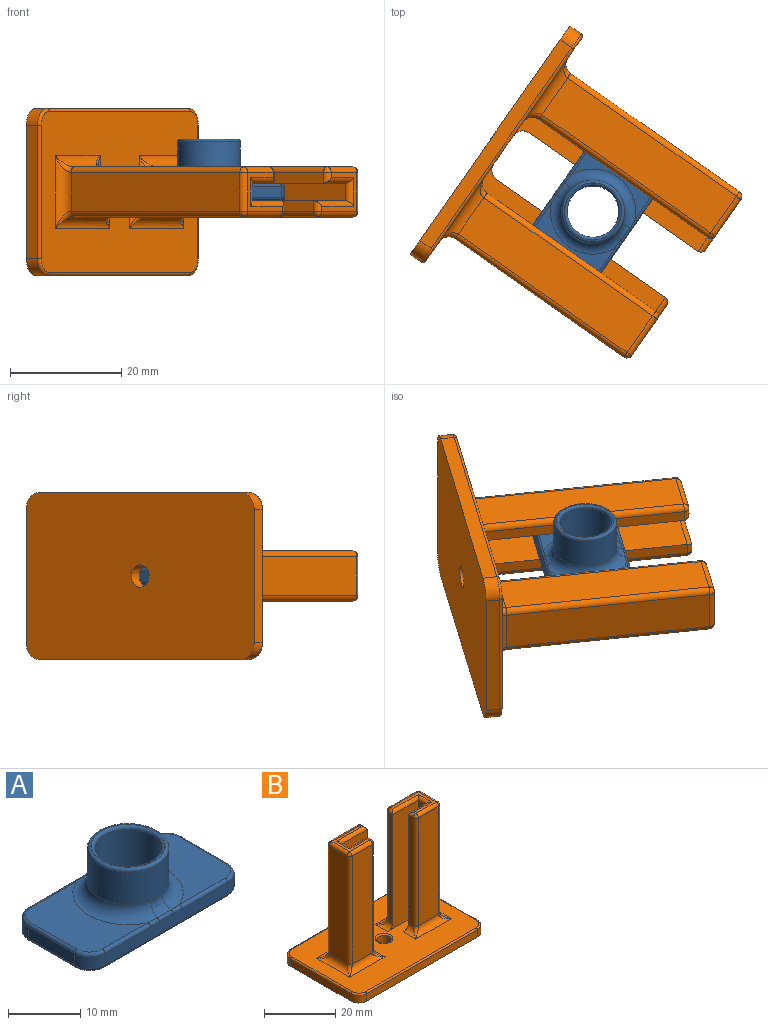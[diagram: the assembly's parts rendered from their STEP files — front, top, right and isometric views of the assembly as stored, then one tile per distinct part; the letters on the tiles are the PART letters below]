
ASSEMBLY  parts=2 mates=1
PART A: 45 faces, bbox 30.5x19.3x11 mm
  f0: plane 14x11.44mm, normal (0,0,1), area 111.3mm2, adj f15,f18,f19,f20,f22,f24
  f1: plane 9x2mm, normal (1,0,0), area 18mm2, adj f2,f9,f31,f38
  f2: cylinder r=3mm len=3mm, axis (0,0,-1), area 9.4mm2, adj f1,f3,f33,f40
  f3: plane 24x2.08mm, normal (0,1,0), area 48.3mm2, adj f2,f4,f24,f26,f28,f30,f32,f41
  f4: cylinder r=3mm len=3mm, axis (0,0,-1), area 9.4mm2, adj f3,f5,f22,f39
  f5: plane 9x2mm, normal (-1,0,0), area 18mm2, adj f4,f6,f20,f37
  f6: cylinder r=3mm len=3mm, axis (0,0,-1), area 9.4mm2, adj f5,f7,f18,f35
  f7: plane 24x2.08mm, normal (0,-1,0), area 48.3mm2, adj f6,f9,f19,f21,f23,f25,f27,f34
  f8: cylinder r=4.6mm len=10mm, axis (0,0,-1), area 289mm2, adj f42,f44
  f9: cylinder r=3mm len=3mm, axis (0,0,-1), area 9.4mm2, adj f1,f7,f29,f36
  f10: plane 14x11.44mm, normal (0,0,1), area 111.3mm2, adj f16,f27,f29,f31,f32,f33
  f11: plane 29x14mm, normal (0,0,-1), area 318.9mm2, adj f34,f35,f36,f37,f38,f39,f40,f41
  f12: cylinder r=5.64mm len=11.28mm, axis (0,0,-1), area 194.9mm2, adj f14,f15,f16,f17,f43
  f13: plane 10.28x10.28mm, normal (0,0,1), area 1.3mm2, adj f42,f43
  f14: bspline ~4.14x2.15mm, area 6.3mm2, adj f12,f15,f16,f28
  f15: torus R=7.64mm, axis (0,0,1), area 54.5mm2, adj f0,f12,f14,f17,f21,f26
  f16: torus R=7.64mm, axis (0,0,1), area 54.5mm2, adj f10,f12,f14,f17,f25,f30
  f17: bspline ~4.14x2.15mm, area 6.3mm2, adj f12,f15,f16,f23
  f18: torus R=2.5mm, axis (0,0,1), area 3.5mm2, adj f0,f6,f19,f20
  f19: cylinder r=0.5mm len=8.94mm, axis (-1,0,0), area 7mm2, adj f0,f7,f18,f21
  f20: cylinder r=0.5mm len=9mm, axis (0,1,0), area 7.1mm2, adj f0,f5,f18,f22
  f21: bspline ~3.04x0.56mm, area 1.2mm2, adj f7,f15,f19,f23
  f22: torus R=2.5mm, axis (0,0,1), area 3.5mm2, adj f0,f4,f20,f24
  f23: bspline ~3.6x0.53mm, area 1.8mm2, adj f7,f17,f21,f25
  f24: cylinder r=0.5mm len=8.94mm, axis (1,0,0), area 7mm2, adj f0,f3,f22,f26
  f25: bspline ~3.41x0.59mm, area 1.2mm2, adj f7,f16,f23,f27
  f26: bspline ~3.41x0.59mm, area 1.2mm2, adj f3,f15,f24,f28
  f27: cylinder r=0.5mm len=8.94mm, axis (-1,0,0), area 7mm2, adj f7,f10,f25,f29
  f28: bspline ~3.6x0.53mm, area 1.8mm2, adj f3,f14,f26,f30
  f29: torus R=2.5mm, axis (0,0,1), area 3.5mm2, adj f9,f10,f27,f31
  f30: bspline ~3.04x0.56mm, area 1.2mm2, adj f3,f16,f28,f32
  f31: cylinder r=0.5mm len=9mm, axis (0,-1,0), area 7.1mm2, adj f1,f10,f29,f33
  f32: cylinder r=0.5mm len=8.94mm, axis (1,0,0), area 7mm2, adj f3,f10,f30,f33
  f33: torus R=2.5mm, axis (0,0,1), area 3.5mm2, adj f2,f10,f31,f32
  f34: cylinder r=0.5mm len=24mm, axis (1,0,0), area 18.8mm2, adj f7,f11,f35,f36
  f35: torus R=2.5mm, axis (0,0,1), area 3.5mm2, adj f6,f11,f34,f37
  f36: torus R=2.5mm, axis (0,0,1), area 3.5mm2, adj f9,f11,f34,f38
  f37: cylinder r=0.5mm len=9mm, axis (0,-1,0), area 7.1mm2, adj f5,f11,f35,f39
  f38: cylinder r=0.5mm len=9mm, axis (0,1,0), area 7.1mm2, adj f1,f11,f36,f40
  f39: torus R=2.5mm, axis (0,0,1), area 3.5mm2, adj f4,f11,f37,f41
  f40: torus R=2.5mm, axis (0,0,1), area 3.5mm2, adj f2,f11,f38,f41
  f41: cylinder r=0.5mm len=24mm, axis (-1,0,0), area 18.8mm2, adj f3,f11,f39,f40
  f42: torus R=5.1mm, axis (0,0,1), area 23.6mm2, adj f8,f13
  f43: torus R=5.14mm, axis (0,0,1), area 26.9mm2, adj f12,f13
  f44: torus R=5.1mm, axis (0,0,1), area 23.6mm2, adj f8,f11
PART B: 88 faces, bbox 50.5x30.5x43 mm
  f0: plane 24x2.5mm, normal (1,0,0), area 60mm2, adj f1,f8,f10,f83
  f1: cylinder r=3mm len=3mm, axis (0,0,-1), area 11.8mm2, adj f0,f2,f10,f81
  f2: plane 44x2.5mm, normal (0,1,0), area 110mm2, adj f1,f3,f10,f79
  f3: cylinder r=3mm len=3mm, axis (0,0,-1), area 11.8mm2, adj f2,f4,f10,f80
  f4: plane 24x2.5mm, normal (-1,0,0), area 60mm2, adj f3,f5,f10,f82
  f5: cylinder r=3mm len=3mm, axis (0,0,-1), area 11.8mm2, adj f4,f6,f10,f84
  f6: plane 44x2.5mm, normal (0,-1,0), area 110mm2, adj f5,f8,f10,f86
  f7: cylinder r=2mm len=4mm, axis (0,0,-1), area 31.4mm2, adj f10,f87
  f8: cylinder r=3mm len=3mm, axis (0,0,-1), area 11.8mm2, adj f0,f6,f10,f85
  f9: plane 49x29mm, normal (0,0,1), area 1060.2mm2, adj f15,f16,f17,f24,f25,f26,f29,f30
  f10: plane 50x30mm, normal (0,0,-1), area 1479.7mm2, adj f0,f1,f2,f3,f4,f5,f6,f7
  f11: plane 37x11mm, normal (0,1,0), area 407mm2, adj f36,f71,f75,f77
  f12: plane 37x7mm, normal (-1,0,0), area 259mm2, adj f38,f65,f70,f71
  f13: plane 37x8mm, normal (0,-1,0), area 296mm2, adj f37,f60,f64,f65
  f14: plane 37x1.9mm, normal (1,0,0), area 70.3mm2, adj f15,f35,f60,f63
  f15: plane 39x9mm, normal (0,1,0), area 273.9mm2, adj f9,f14,f16,f35,f66
  f16: plane 39x3.2mm, normal (1,0,0), area 124.8mm2, adj f9,f15,f17,f69
  f17: plane 39x12mm, normal (0,-1,0), area 390.9mm2, adj f9,f16,f18,f34,f72
  f18: plane 37x1.9mm, normal (1,0,0), area 70.3mm2, adj f17,f34,f74,f77
  f19: plane 11x7mm, normal (0,0,1), area 22.3mm2, adj f63,f64,f66,f69,f70,f72,f74,f75
  f20: plane 37x8mm, normal (0,-1,0), area 296mm2, adj f30,f48,f54,f57
  f21: plane 37x7mm, normal (1,0,0), area 259mm2, adj f31,f51,f55,f57
  f22: plane 37x11mm, normal (0,1,0), area 407mm2, adj f32,f43,f50,f51
  f23: plane 37x1.9mm, normal (-1,0,0), area 70.3mm2, adj f24,f33,f42,f43
  f24: plane 39x12mm, normal (0,-1,0), area 390.9mm2, adj f9,f23,f25,f33,f39
  f25: plane 39x3.2mm, normal (-1,0,0), area 124.8mm2, adj f9,f24,f26,f41
  f26: plane 39x9mm, normal (0,1,0), area 273.9mm2, adj f9,f25,f27,f29,f45
  f27: plane 37x1.9mm, normal (-1,0,0), area 70.3mm2, adj f26,f29,f48,f49
  f28: plane 11x7mm, normal (0,0,1), area 22.3mm2, adj f39,f41,f42,f45,f49,f50,f54,f55
  f29: cylinder r=2mm len=4.9mm, axis (0,-1,0), area 9.4mm2, adj f9,f26,f27,f44
  f30: cylinder r=2mm len=14mm, axis (1,0,0), area 32mm2, adj f9,f20,f44,f58
  f31: cylinder r=2mm len=13mm, axis (0,1,0), area 28.8mm2, adj f9,f21,f47,f58
  f32: cylinder r=2mm len=17mm, axis (-1,0,0), area 41.4mm2, adj f9,f22,f40,f47
  f33: cylinder r=2mm len=4.9mm, axis (0,-1,0), area 9.4mm2, adj f9,f23,f24,f40
  f34: cylinder r=2mm len=4.9mm, axis (0,1,0), area 9.4mm2, adj f9,f17,f18,f78
  f35: cylinder r=2mm len=4.9mm, axis (0,1,0), area 9.4mm2, adj f9,f14,f15,f59
  f36: cylinder r=2mm len=17mm, axis (-1,0,0), area 41.4mm2, adj f9,f11,f68,f78
  f37: cylinder r=2mm len=14mm, axis (1,0,0), area 32mm2, adj f9,f13,f59,f62
  f38: cylinder r=2mm len=13mm, axis (0,-1,0), area 28.8mm2, adj f9,f12,f62,f68
  f39: cylinder r=1mm len=11mm, axis (-1,0,0), area 15.7mm2, adj f24,f28,f41,f42
  f40: bspline ~3x3mm, area 3.6mm2, adj f32,f33,f43
  f41: cylinder r=1mm len=5.2mm, axis (0,1,0), area 6.2mm2, adj f25,f28,f39,f45
  f42: cylinder r=1mm len=1.9mm, axis (0,1,0), area 2.4mm2, adj f23,f28,f39,f46
  f43: cylinder r=1mm len=37mm, axis (0,0,-1), area 58.1mm2, adj f22,f23,f40,f46
  f44: bspline ~3x3mm, area 3.6mm2, adj f29,f30,f48
  f45: cylinder r=1mm len=8mm, axis (1,0,0), area 11mm2, adj f26,f28,f41,f49
  f46: sphere r=1mm, area 1.6mm2, adj f42,f43,f50
  f47: bspline ~3x3mm, area 3.6mm2, adj f31,f32,f51
  f48: cylinder r=1mm len=37mm, axis (0,0,-1), area 58.1mm2, adj f20,f27,f44,f52
  f49: cylinder r=1mm len=1.9mm, axis (0,1,0), area 2.4mm2, adj f27,f28,f45,f52
  f50: cylinder r=1mm len=11mm, axis (1,0,0), area 17.3mm2, adj f22,f28,f46,f53
  f51: cylinder r=1mm len=37mm, axis (0,0,-1), area 58.1mm2, adj f21,f22,f47,f53
  f52: sphere r=1mm, area 1.6mm2, adj f48,f49,f54
  f53: sphere r=1mm, area 1.6mm2, adj f50,f51,f55
  f54: cylinder r=1mm len=8mm, axis (-1,0,0), area 12.6mm2, adj f20,f28,f52,f56
  f55: cylinder r=1mm len=7mm, axis (0,-1,0), area 11mm2, adj f21,f28,f53,f56
  f56: sphere r=1mm, area 1.6mm2, adj f54,f55,f57
  f57: cylinder r=1mm len=37mm, axis (0,0,-1), area 58.1mm2, adj f20,f21,f56,f58
  f58: bspline ~3x3mm, area 3.6mm2, adj f30,f31,f57
  f59: bspline ~3x3mm, area 3.6mm2, adj f35,f37,f60
  f60: cylinder r=1mm len=37mm, axis (0,0,-1), area 58.1mm2, adj f13,f14,f59,f61
  f61: sphere r=1mm, area 1.6mm2, adj f60,f63,f64
  f62: bspline ~3x3mm, area 3.6mm2, adj f37,f38,f65
  f63: cylinder r=1mm len=1.9mm, axis (0,-1,0), area 2.4mm2, adj f14,f19,f61,f66
  f64: cylinder r=1mm len=8mm, axis (-1,0,0), area 12.6mm2, adj f13,f19,f61,f67
  f65: cylinder r=1mm len=37mm, axis (0,0,-1), area 58.1mm2, adj f12,f13,f62,f67
  f66: cylinder r=1mm len=8mm, axis (1,0,0), area 11mm2, adj f15,f19,f63,f69
  f67: sphere r=1mm, area 1.6mm2, adj f64,f65,f70
  f68: bspline ~3x3mm, area 3.6mm2, adj f36,f38,f71
  f69: cylinder r=1mm len=5.2mm, axis (0,-1,0), area 6.2mm2, adj f16,f19,f66,f72
  f70: cylinder r=1mm len=7mm, axis (0,1,0), area 11mm2, adj f12,f19,f67,f73
  f71: cylinder r=1mm len=37mm, axis (0,0,-1), area 58.1mm2, adj f11,f12,f68,f73
  f72: cylinder r=1mm len=11mm, axis (-1,0,0), area 15.7mm2, adj f17,f19,f69,f74
  f73: sphere r=1mm, area 1.6mm2, adj f70,f71,f75
  f74: cylinder r=1mm len=1.9mm, axis (0,-1,0), area 2.4mm2, adj f18,f19,f72,f76
  f75: cylinder r=1mm len=11mm, axis (1,0,0), area 17.3mm2, adj f11,f19,f73,f76
  f76: sphere r=1mm, area 1.6mm2, adj f74,f75,f77
  f77: cylinder r=1mm len=37mm, axis (0,0,-1), area 58.1mm2, adj f11,f18,f76,f78
  f78: bspline ~3x3mm, area 3.6mm2, adj f34,f36,f77
  f79: cylinder r=0.5mm len=44mm, axis (1,0,0), area 34.6mm2, adj f2,f9,f80,f81
  f80: torus R=2.5mm, axis (0,0,1), area 3.5mm2, adj f3,f9,f79,f82
  f81: torus R=2.5mm, axis (0,0,1), area 3.5mm2, adj f1,f9,f79,f83
  f82: cylinder r=0.5mm len=24mm, axis (0,1,0), area 18.8mm2, adj f4,f9,f80,f84
  f83: cylinder r=0.5mm len=24mm, axis (0,-1,0), area 18.8mm2, adj f0,f9,f81,f85
  f84: torus R=2.5mm, axis (0,0,1), area 3.5mm2, adj f5,f9,f82,f86
  f85: torus R=2.5mm, axis (0,0,1), area 3.5mm2, adj f8,f9,f83,f86
  f86: cylinder r=0.5mm len=44mm, axis (-1,0,0), area 34.6mm2, adj f6,f9,f84,f85
  f87: torus R=2.5mm, axis (0,0,1), area 10.8mm2, adj f7,f9
PLACE A rot(axis=(0,0,-1),125deg) t=(18.13,11.44,-16.56)mm
PLACE B rot(axis=(-0.35,0.66,-0.66),141.9deg) t=(-0.35,24.26,32.44)mm
MATE slider B.f16 <-> A.f5  axis (-0.57,-0.82,0) through (26.74,23.72,-15.06)mm
